# Revit family: 0043437_3000K
name_source: partatom
category: Lighting Fixtures
revit_build: Autodesk Revit 2017 (Build: 20190507_1515(x64)
units: mm (PartAtom-declared; Revit-internal decimal feet)

## family parameters
Cut with Voids When Loaded = No
Host = Face
Light Source = Yes
OmniClass Number = 23.80.70.00
OmniClass Title = Lighting
Part Type = Normal
Room Calculation Point = No
Round Connector Dimension = Use Diameter
Shared = No

## types (2) — shared parameters
Apparent Load = 18 VA
Assembly Code = D5020200
AssetType = Fixed
BOTTOM_HEIGHT_SYL = 81 mm  [stored 0.265748 ft]
BOTTOM_R_SYL = 150 mm
ClassificationName = Uniclass2015
ClassificationValue = EF_70_80
Color Filter = 16777215
Default Elevation = 1219 mm
Dimming Lamp Color Temperature Shift = <None>
DocumentationLiterature = http://www.sylvania-lighting.com
ElectricShockClassification = Class I
Emit Shape Visible in Rendering = No
Emit from Circle Diameter = 610 mm
IfcExportAs = IfcLightFixtureType
IfcExportType = IfcLightFixtureType
ImpactProtectionIndex = IK03
IngressProtection = IP44
Keynote = 16500
LUM_H_SYL = 96 mm  [stored 0.314961 ft]
LUM_R_HEIGHT_SYL = 66 mm  [stored 0.216535 ft]
LUM_R_SYL = 165 mm
Lamp = LED
LampColourRenderingIndex = 80
LampMacAdamStep = 6
LampNominalLuminous = 1400 lm
LampsType = LED
LuminousEfficacy = 78 lm/W
Manufacturer = Feilo Sylvania
ManufacturerName = Feilo Sylvania
Material = steel housing, polypropylene diffuser
Material_1_SYL = <By Category>
Material_2_SYL = <By Category>
Material_3_SYL = <By Category>
Material_4_SYL = <By Category>
Model = Start eco Surface IP44 PIR 1400lm 830/840 DualTone
ModelNumber = 0043437
ModelReference = Start eco Surface IP44 PIR 1400lm 830/840 DualTone
Name = Start eco Surface IP44 PIR 1400lm 830/840 DualTone
NominalDepth = 330 mm
NominalHeight = 108 mm
NominalLength = 330 mm
PowerConsumption = 18 W
PowerFactor = 0.7
SENSOR_SYL = 12 mm  [stored 0.0393701 ft]
Tilt Angle = -90.00°
Type Image = <None>
TypeName = Start eco Surface IP44 PIR 1400lm 830/840 DualTone
URL = http://www.sylvania-lighting.com
Voltage = 0 V
Weight = 3.54 kg
YIN_180_SYL = No
YIN_250_SYL = No
YIN_330_SYL = Yes
YIN_360_SYL = No
zero-valued in all types: Cost

## per-type parameters (varying)
| type | LampColourTemperature | Photometric Web File |
| 0043437 STRT ECO SURF IP44 PIR 1400LM 830 DT | 3000 K | 0043437_3000K.IES |
| 0043437 STRT ECO SURF IP44 PIR 1400LM 840 DT | 4000 K | 0043437_4000K.ies |

note: [stored X ft] marks values corroborated as IEEE doubles in the binary element streams (Revit-internal decimal feet)

## geometry (parser evidence)
native form markers: Sweep x2
no freeform markers — native parametric forms only
